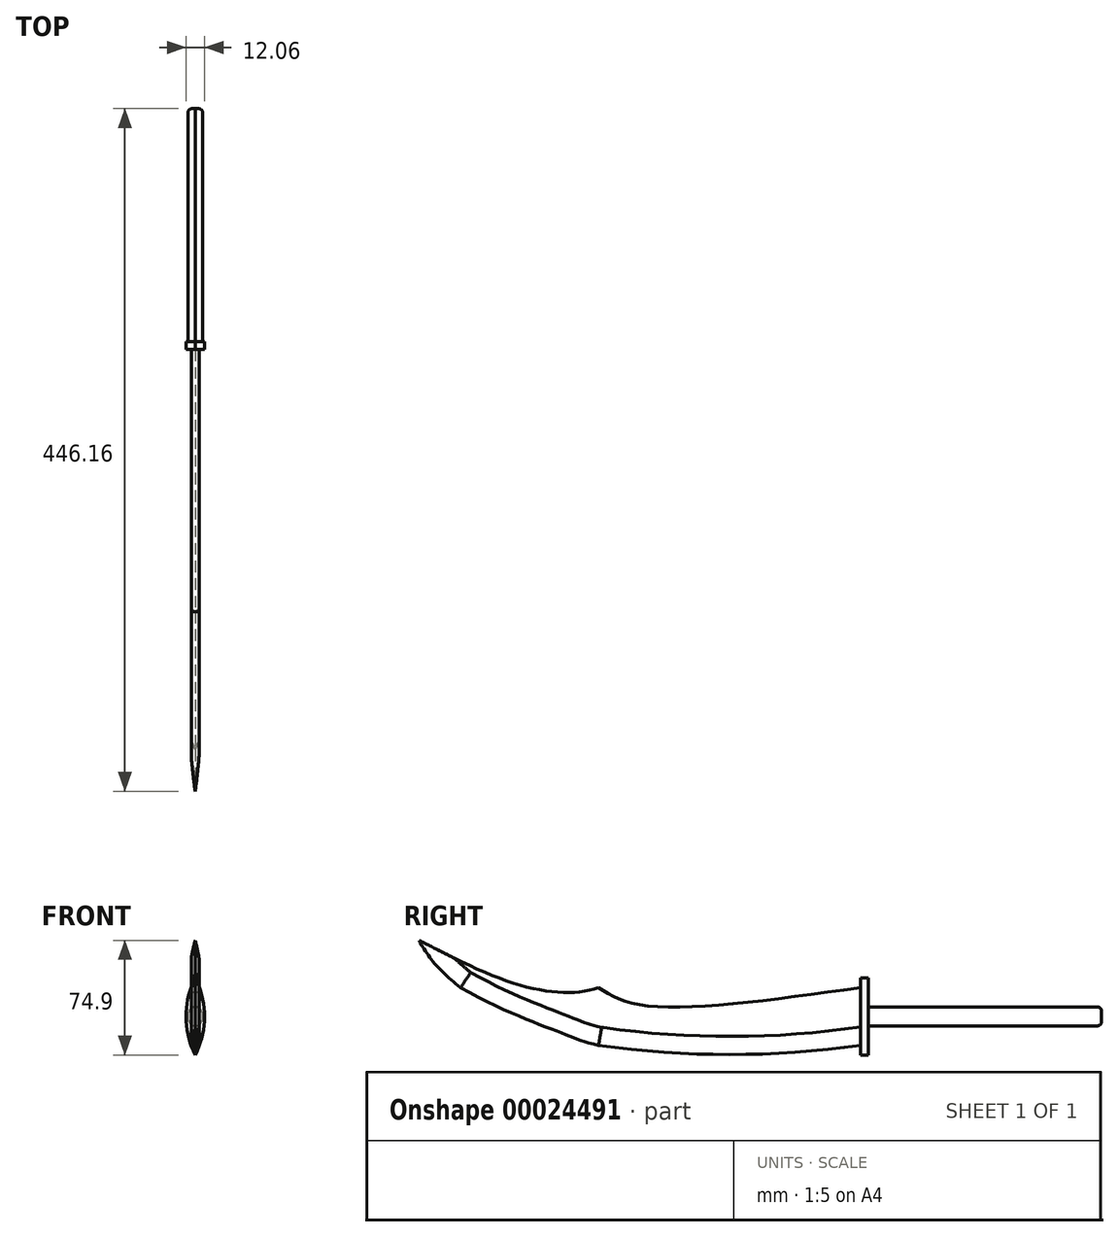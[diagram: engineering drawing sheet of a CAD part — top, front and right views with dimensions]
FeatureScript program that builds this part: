
annotation { "Feature Type Name" : "Feature", "Feature Type Description" : "" }
export const myFeature = defineFeature(function(context is Context, id is Id, definition is map)
    precondition{}
    {
        {
            var Q0;
            Q0=qCreatedBy(makeId("Right.planeOp"),FACE);
            var sketch = newSketch(context, id + "F0", { "sketchPlane" : qUnion([Q0])});
            skFitSpline(sketch, "E0", {"points": [v(0, 0) * mm, v(68.24, -30.54) * mm, v(90.29, -37.7) * mm], "startDerivative": vector(137, -76.78) * mm, "endDerivative": vector(85.47, -17.15) * mm});
            skFitSpline(sketch, "E1", {"points": [v(-139.2, -1.69) * mm, v(-77.69, 49.64) * mm, v(21.2, 7.75) * mm, v(90.29, 0) * mm], "startDerivative": vector(362.9, 286.6) * mm, "endDerivative": vector(168.08, 61.78) * mm});
            skArc(sketch, "E2", {"start": v(90.29, -37.7) * mm, "mid": v(175.95, -43.78) * mm, "end": v(261.61, -37.7) * mm});
            skLineSegment(sketch, "E3", {"start": v(261.61, 0) * mm, "end": v(261.61, -37.7) * mm});
            skFitSpline(sketch, "E4", {"points": [v(261.61, 0) * mm, v(118.22, -11.5) * mm, v(90.29, 0) * mm], "startDerivative": vector(-250.32, -35.06) * mm, "endDerivative": vector(-70, 44.97) * mm});
            skFitSpline(sketch, "E5", {"points": [v(0, 0) * mm, v(-17.27, 16.05) * mm, v(-27.07, 30.85) * mm], "startDerivative": vector(-35.24, 29.48) * mm, "endDerivative": vector(-18.5, 32.28) * mm});
            skSolve(sketch);
        }
        {
            var Q0;
            Q0 = qSketchRegion(id + "F0", true);
            extrude(context, id + "F1", {"entities" : qUnion([Q0]), "depth" : 5.08 * mm});
        }
        {
            var Q0;
            Q0=makeQuery(id+"F1.opExtrude","SWEPT_FACE",FACE,{"disambiguationData":[OSD([sQuery(id+"F0.wireOp",EDGE,"E3")])]});
            var sketch = newSketch(context, id + "F2", { "sketchPlane" : qUnion([Q0])});
            skLineSegment(sketch, "E6", {"start": v(-5.08, -25.73) * mm, "end": v(-2.54, -37.7) * mm});
            skLineSegment(sketch, "E7", {"start": v(0, -25.73) * mm, "end": v(-2.54, -37.7) * mm});
            skSolve(sketch);
        }
        {
            var Q0;
            {var subQ0=sQuery(id+"F2.wireOp",EDGE,"E6");Q0=makeQuery(id+"F2.imprint","IMPRINT",FACE,{"disambiguationData":[TD([[makeQuery(id+"F2.imprint","IMPRINT",EDGE,{"derivedFrom":subQ0}),-1.0]])]});}
            var Q1;
            {var subQ0=sQuery(id+"F2.wireOp",EDGE,"E7");Q1=makeQuery(id+"F2.imprint","IMPRINT",FACE,{"disambiguationData":[TD([[makeQuery(id+"F2.imprint","IMPRINT",EDGE,{"derivedFrom":subQ0}),1.0]])]});}
            var Q2;
            Q2=makeQuery(id+"F1.opExtrude","CAP_EDGE",EDGE,{"disambiguationData":[OSD([sQuery(id+"F0.wireOp",EDGE,"E5")])],"isStart":true});
            var Q3;
            Q3=makeQuery(id+"F1.opExtrude","CAP_EDGE",EDGE,{"disambiguationData":[OSD([sQuery(id+"F0.wireOp",EDGE,"E2")])],"isStart":true});
            var Q4;
            Q4=makeQuery(id+"F1.opExtrude","CAP_EDGE",EDGE,{"disambiguationData":[OSD([sQuery(id+"F0.wireOp",EDGE,"E0")])],"isStart":true});
            sweep(context, id + "F3", {"operationType" : NewBodyOperationType.REMOVE, "profiles" : qUnion([Q0, Q1]), "path" : qUnion([Q2, Q3, Q4])});
        }
        {
            var Q0;
            Q0=makeQuery(id+"F1.opExtrude","SWEPT_FACE",FACE,{"disambiguationData":[OSD([sQuery(id+"F0.wireOp",EDGE,"E3")])]});
            var sketch = newSketch(context, id + "F4", { "sketchPlane" : qUnion([Q0])});
            skLineSegment(sketch, "E8", {"start": v(-2.54, 0) * mm, "end": v(-2.54, 6.35) * mm});
            skPoint(sketch, "E8.endSnap0", {"position": v(-2.54, 0) * mm});
            skLineSegment(sketch, "E9", {"start": v(-2.54, -37.7) * mm, "end": v(-2.54, -44.05) * mm});
            skArc(sketch, "E10", {"start": v(-2.54, 6.35) * mm, "mid": v(-8.64, -18.85) * mm, "end": v(-2.54, -44.05) * mm});
            skArc(sketch, "E11", {"start": v(-2.54, -44.05) * mm, "mid": v(3.42, -18.85) * mm, "end": v(-2.54, 6.35) * mm});
            skSolve(sketch);
        }
        {
            var Q0;
            Q0 = qSketchRegion(id + "F4", true);
            extrude(context, id + "F5", {"entities" : qUnion([Q0]), "operationType" : NewBodyOperationType.ADD, "depth" : 5.08 * mm});
        }
        {
            var Q0;
            Q0=makeQuery(id+"F5.opExtrude","CAP_FACE",FACE,{"disambiguationData":[OSD([sQuery(id+"F4.wireOp",EDGE,"E10"),sQuery(id+"F4.wireOp",EDGE,"E11")])],"isStart":false});
            var sketch = newSketch(context, id + "F6", { "sketchPlane" : qUnion([Q0])});
            skLineSegment(sketch, "E12", {"start": v(-2.54, 6.35) * mm, "end": v(-2.54, -12.7) * mm});
            skLineSegment(sketch, "E13", {"start": v(-2.54, -44.05) * mm, "end": v(-2.54, -25) * mm});
            skLineSegment(sketch, "E14", {"start": v(-2.54, -12.7) * mm, "end": v(3.08, -12.7) * mm});
            skLineSegment(sketch, "E15", {"start": v(-2.54, -12.7) * mm, "end": v(-8.3, -12.7) * mm});
            skLineSegment(sketch, "E16", {"start": v(-2.54, -25) * mm, "end": v(3.08, -25) * mm});
            skLineSegment(sketch, "E17", {"start": v(-2.54, -25) * mm, "end": v(-8.3, -25) * mm});
            skLineSegment(sketch, "E18", {"start": v(-7.38, -25) * mm, "end": v(-7.38, -12.7) * mm});
            skLineSegment(sketch, "E19", {"start": v(2.15, -12.7) * mm, "end": v(2.15, -25) * mm});
            skSolve(sketch);
        }
        {
            var Q0;
            Q0 = qSketchRegion(id + "F6", true);
            extrude(context, id + "F7", {"entities" : qUnion([Q0]), "operationType" : NewBodyOperationType.ADD, "depth" : 152.4 * mm});
        }
        {
            var Q0;
            Q0=makeQuery(id+"F7.opExtrude","SWEPT_EDGE",EDGE,{"disambiguationData":[OSD([sQuery(id+"F6.wireOp",EDGE,"E15"),sQuery(id+"F6.wireOp",EDGE,"E18")])]});
            var Q1;
            Q1=makeQuery(id+"F7.opExtrude","SWEPT_EDGE",EDGE,{"disambiguationData":[OSD([sQuery(id+"F6.wireOp",EDGE,"E16"),sQuery(id+"F6.wireOp",EDGE,"E19")])]});
            var Q2;
            Q2=makeQuery(id+"F7.opExtrude","SWEPT_EDGE",EDGE,{"disambiguationData":[OSD([sQuery(id+"F6.wireOp",EDGE,"E14"),sQuery(id+"F6.wireOp",EDGE,"E19")])]});
            var Q3;
            Q3=makeQuery(id+"F7.opExtrude","SWEPT_EDGE",EDGE,{"disambiguationData":[OSD([sQuery(id+"F6.wireOp",EDGE,"E17"),sQuery(id+"F6.wireOp",EDGE,"E18")])]});
            fillet(context, id + "F8", {"entities" : qUnion([Q0, Q1, Q2, Q3]), "radius" : 5.08 * mm, "tangentPropagation" : true, "allowEdgeOverflow" : false});
        }
        {
            var Q0;
            Q0=makeQuery(id+"F7.opExtrude","CAP_EDGE",EDGE,{"disambiguationData":[OSD([sQuery(id+"F6.wireOp",EDGE,"E19")])],"isStart":false});
            var Q1;
            Q1=makeQuery(id+"F7.opExtrude","CAP_EDGE",EDGE,{"disambiguationData":[OSD([sQuery(id+"F6.wireOp",EDGE,"E18")])],"isStart":false});
            fillet(context, id + "F9", {"entities" : qUnion([Q0, Q1]), "radius" : 2.54 * mm, "tangentPropagation" : true, "allowEdgeOverflow" : false});
        }
    });
